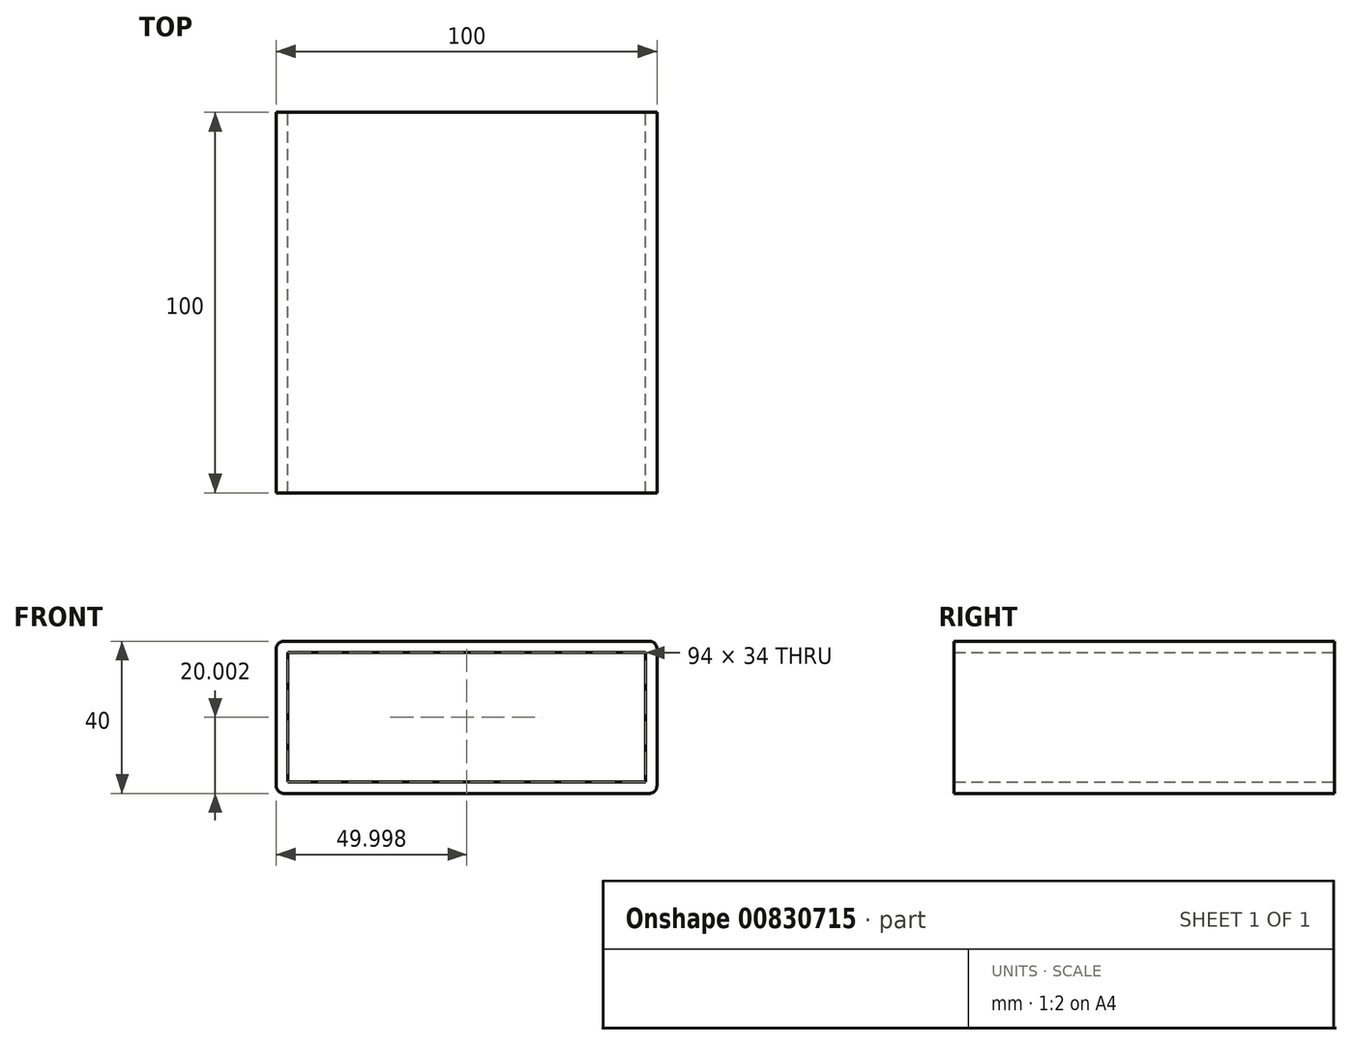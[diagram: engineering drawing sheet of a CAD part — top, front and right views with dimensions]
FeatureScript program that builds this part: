
annotation { "Feature Type Name" : "Feature", "Feature Type Description" : "" }
export const myFeature = defineFeature(function(context is Context, id is Id, definition is map)
    precondition{}
    {
        {
            assignVariable(context, id + "F0", {"name" : "TubeWidth", "anyValue" : 100});
        }
        {
            assignVariable(context, id + "F1", {"name" : "TubeHeight", "anyValue" : 40});
        }
        {
            assignVariable(context, id + "F2", {"name" : "ShortSideSize", "anyValue" : 460 - getVariable(context, 'TubeHeight') * 4});
        }
        {
            var Q0;
            Q0=qCreatedBy(makeId("Front.planeOp"),FACE);
            var sketch = newSketch(context, id + "F3", { "sketchPlane" : qUnion([Q0])});
            skPoint(sketch, "E0.middle", {"position": v(-14.96, 34.76) * mm});
            skLineSegment(sketch, "E1.bottom", {"start": v(-17.25, -51.74) * mm, "end": v(78.75, -51.74) * mm});
            skLineSegment(sketch, "E1.top", {"start": v(-17.25, -11.74) * mm, "end": v(78.75, -11.74) * mm});
            skLineSegment(sketch, "E1.left", {"start": v(-19.25, -49.74) * mm, "end": v(-19.25, -13.74) * mm});
            skLineSegment(sketch, "E1.right", {"start": v(80.75, -49.74) * mm, "end": v(80.75, -13.74) * mm});
            skPoint(sketch, "E2.visualSharp", {"position": v(-19.25, -11.74) * mm});
            skArc(sketch, "E2.filletArc", {"start": v(-17.25, -11.74) * mm, "mid": v(-18.67, -12.32) * mm, "end": v(-19.25, -13.74) * mm});
            skPoint(sketch, "E3.visualSharp", {"position": v(80.75, -11.74) * mm});
            skArc(sketch, "E3.filletArc", {"start": v(80.75, -13.74) * mm, "mid": v(80.16, -12.32) * mm, "end": v(78.75, -11.74) * mm});
            skPoint(sketch, "E4.visualSharp", {"position": v(80.75, -51.74) * mm});
            skArc(sketch, "E4.filletArc", {"start": v(78.75, -51.74) * mm, "mid": v(80.16, -51.15) * mm, "end": v(80.75, -49.74) * mm});
            skPoint(sketch, "E5.visualSharp", {"position": v(-19.25, -51.74) * mm});
            skArc(sketch, "E5.filletArc", {"start": v(-19.25, -49.74) * mm, "mid": v(-18.67, -51.15) * mm, "end": v(-17.25, -51.74) * mm});
            skLineSegment(sketch, "E6.0", {"start": v(-17.25, 46.26) * mm, "end": v(-17.25, 46.26) * mm});
            skLineSegment(sketch, "E6.2", {"start": v(-17.25, -49.74) * mm, "end": v(-17.25, -49.74) * mm});
            skLineSegment(sketch, "E6.4", {"start": v(18.75, -49.74) * mm, "end": v(18.75, -49.74) * mm});
            skLineSegment(sketch, "E6.7", {"start": v(18.75, 46.26) * mm, "end": v(18.75, 46.26) * mm});
            skLineSegment(sketch, "E7.0", {"start": v(77.75, -48.74) * mm, "end": v(77.75, -14.74) * mm});
            skLineSegment(sketch, "E7.1", {"start": v(-16.25, -48.74) * mm, "end": v(77.75, -48.74) * mm});
            skLineSegment(sketch, "E7.2", {"start": v(-16.25, -48.74) * mm, "end": v(-16.25, -14.74) * mm});
            skLineSegment(sketch, "E7.3", {"start": v(-16.25, -14.74) * mm, "end": v(77.75, -14.74) * mm});
            skSolve(sketch);
        }
        {
            var Q0;
            Q0 = qSketchRegion(id + "F3", true);
            extrude(context, id + "F4", {"entities" : qUnion([Q0]), "endBound" : BoundingType.SYMMETRIC, "depth" : (getVariable(context, 'ShortSideSize') - 2 * getVariable(context, 'TubeWidth')) * mm, "offsetDistance" : 25 * mm});
        }
        {
            var Q0;
            Q0=makeQuery(id+"F4.opExtrude","SWEPT_BODY",BODY,{"disambiguationData":[OSD([sQuery(id+"F3.wireOp",EDGE,"E1.bottom"),sQuery(id+"F3.wireOp",EDGE,"E1.top"),sQuery(id+"F3.wireOp",EDGE,"E1.left"),sQuery(id+"F3.wireOp",EDGE,"E1.right"),sQuery(id+"F3.wireOp",EDGE,"E2.filletArc"),sQuery(id+"F3.wireOp",EDGE,"E3.filletArc"),sQuery(id+"F3.wireOp",EDGE,"E4.filletArc"),sQuery(id+"F3.wireOp",EDGE,"E5.filletArc"),sQuery(id+"F3.wireOp",EDGE,"E7.0"),sQuery(id+"F3.wireOp",EDGE,"E7.1"),sQuery(id+"F3.wireOp",EDGE,"E7.2"),sQuery(id+"F3.wireOp",EDGE,"E7.3")])]});
            transform(context, id + "F5", {"entities" : qUnion([Q0]), "transformType" : TransformType.TRANSLATION_3D, "dx" : 0 * mm, "dy" : 0 * mm, "dz" : 0 * mm, "makeCopy" : true});
        }
        {
            var Q0;
            Q0=makeQuery(id+"F5.opPattern","COPY",BODY,{"derivedFrom":makeQuery(id+"F4.opExtrude","SWEPT_BODY",BODY,{"disambiguationData":[OSD([sQuery(id+"F3.wireOp",EDGE,"E1.bottom"),sQuery(id+"F3.wireOp",EDGE,"E1.top"),sQuery(id+"F3.wireOp",EDGE,"E1.left"),sQuery(id+"F3.wireOp",EDGE,"E1.right"),sQuery(id+"F3.wireOp",EDGE,"E2.filletArc"),sQuery(id+"F3.wireOp",EDGE,"E3.filletArc"),sQuery(id+"F3.wireOp",EDGE,"E4.filletArc"),sQuery(id+"F3.wireOp",EDGE,"E5.filletArc"),sQuery(id+"F3.wireOp",EDGE,"E7.0"),sQuery(id+"F3.wireOp",EDGE,"E7.1"),sQuery(id+"F3.wireOp",EDGE,"E7.2"),sQuery(id+"F3.wireOp",EDGE,"E7.3")])]}),"instanceName":"1"});
            deleteBodies(context, id + "F6", {"entities" : qUnion([Q0])});
        }
    });
